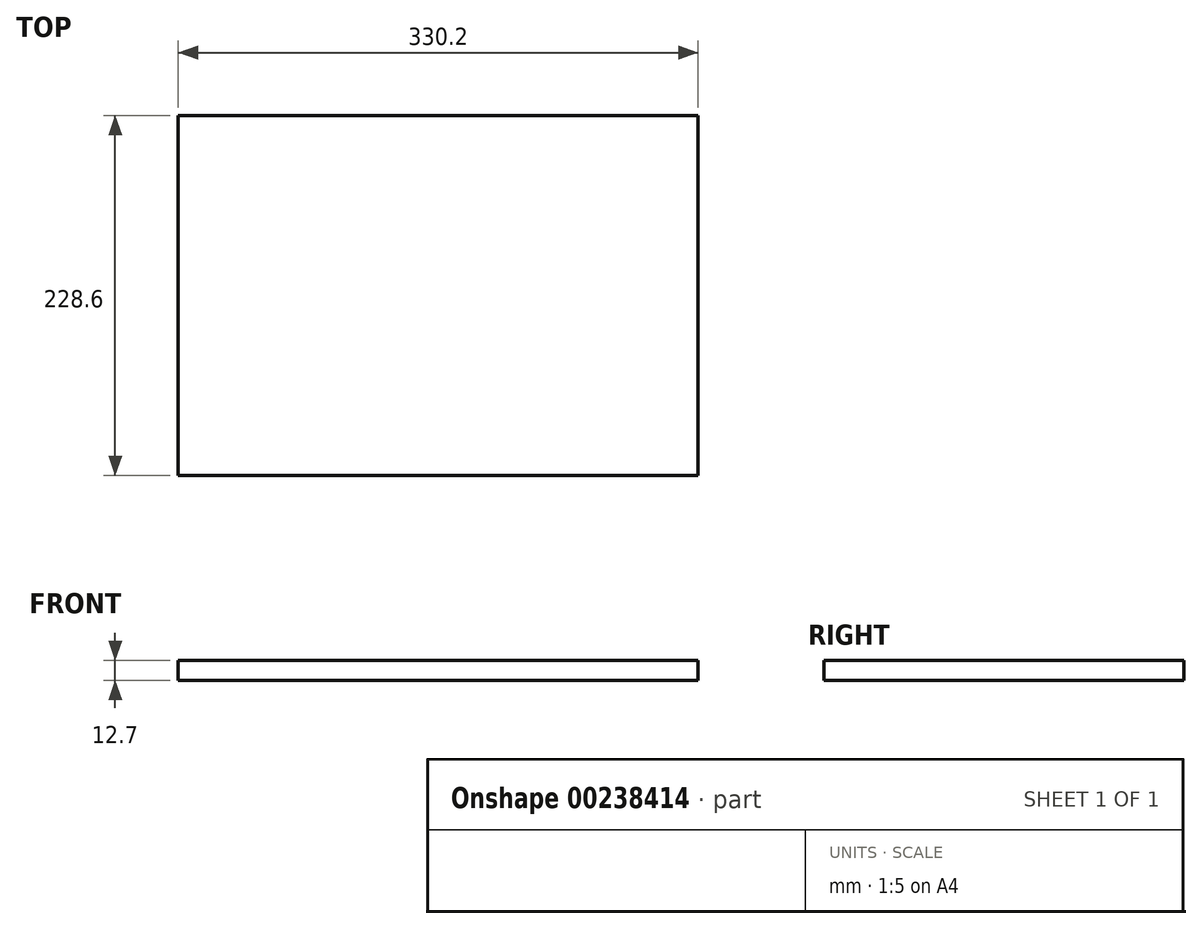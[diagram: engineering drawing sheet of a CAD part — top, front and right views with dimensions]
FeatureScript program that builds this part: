
annotation { "Feature Type Name" : "Feature", "Feature Type Description" : "" }
export const myFeature = defineFeature(function(context is Context, id is Id, definition is map)
    precondition{}
    {
        {
            var Q0;
            Q0=qCreatedBy(makeId("Top.planeOp"),FACE);
            var sketch = newSketch(context, id + "F0", { "sketchPlane" : qUnion([Q0])});
            skLineSegment(sketch, "E0.bottom", {"start": v(165.1, 114.3) * mm, "end": v(-165.1, 114.3) * mm});
            skLineSegment(sketch, "E0.top", {"start": v(165.1, -114.3) * mm, "end": v(-165.1, -114.3) * mm});
            skLineSegment(sketch, "E0.left", {"start": v(165.1, 114.3) * mm, "end": v(165.1, -114.3) * mm});
            skLineSegment(sketch, "E0.right", {"start": v(-165.1, 114.3) * mm, "end": v(-165.1, -114.3) * mm});
            skPoint(sketch, "E0.middle", {"position": v(0, 0) * mm});
            skSolve(sketch);
        }
        {
            var Q0;
            Q0 = qSketchRegion(id + "F0", true);
            extrude(context, id + "F1", {"entities" : qUnion([Q0]), "depth" : 12.7 * mm});
        }
    });
